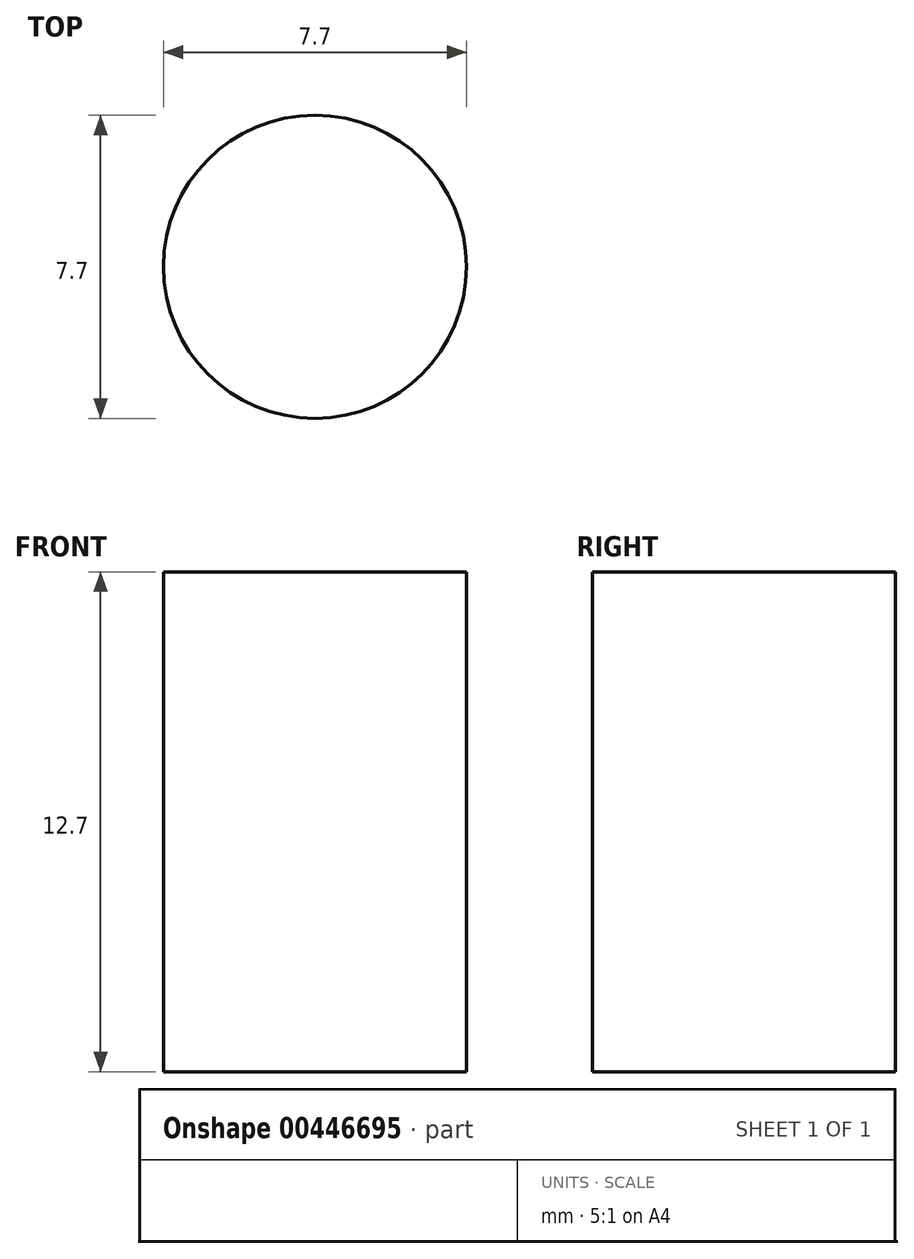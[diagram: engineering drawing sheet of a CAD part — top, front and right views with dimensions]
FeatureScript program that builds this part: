
annotation { "Feature Type Name" : "Feature", "Feature Type Description" : "" }
export const myFeature = defineFeature(function(context is Context, id is Id, definition is map)
    precondition{}
    {
        {
            var Q0;
            Q0=qCreatedBy(makeId("Top.planeOp"),FACE);
            var sketch = newSketch(context, id + "F0", { "sketchPlane" : qUnion([Q0])});
            skCircle(sketch, "E0", {"center": v(0, 0) * mm, "radius": 3.85 * mm});
            skSolve(sketch);
        }
        {
            var Q0;
            Q0 = qSketchRegion(id + "F0", true);
            extrude(context, id + "F1", {"entities" : qUnion([Q0]), "depth" : 12.7 * mm});
        }
    });
